# Revit family: Haworth_Openest_PrivacyBooth
name_source: partatom
category: Furniture
revit_build: Autodesk Revit 2018 (Build: 20170223_1515(x64)
units: mm (PartAtom-declared; Revit-internal decimal feet)

## family parameters
Always vertical = Yes
Cut with Voids When Loaded = No
OmniClass Number = 23.40.20.00
OmniClass Title = General Furniture and Specialties
Room Calculation Point = No
Shared = No
Work Plane-Based = No

## types (1)
- Privacy Booth
    Actual Depth = 5' - 7 1/2"
    Actual Width = 7' - 10"
    Assembly Code = E2020200
    Coat Hook = No
    Description = Haworth - Openest - Privacy Booth
    Hideaway Power Module = No
    Manufacturer = Haworth
    Model = HOAE
    Pillows = Yes
    Rectangular Pillow = No
    Revision No. = 2
    Soft Storage = Yes
    Square Pillow = Yes
    Sustainability Info = https://www.haworth.com
    URL = http://www.haworth.com
    URL - Product = https://www.haworth.com
    Warranty = http://www.haworth.com

## geometry (parser evidence)
native form markers: Sweep x27
no freeform markers — native parametric forms only
